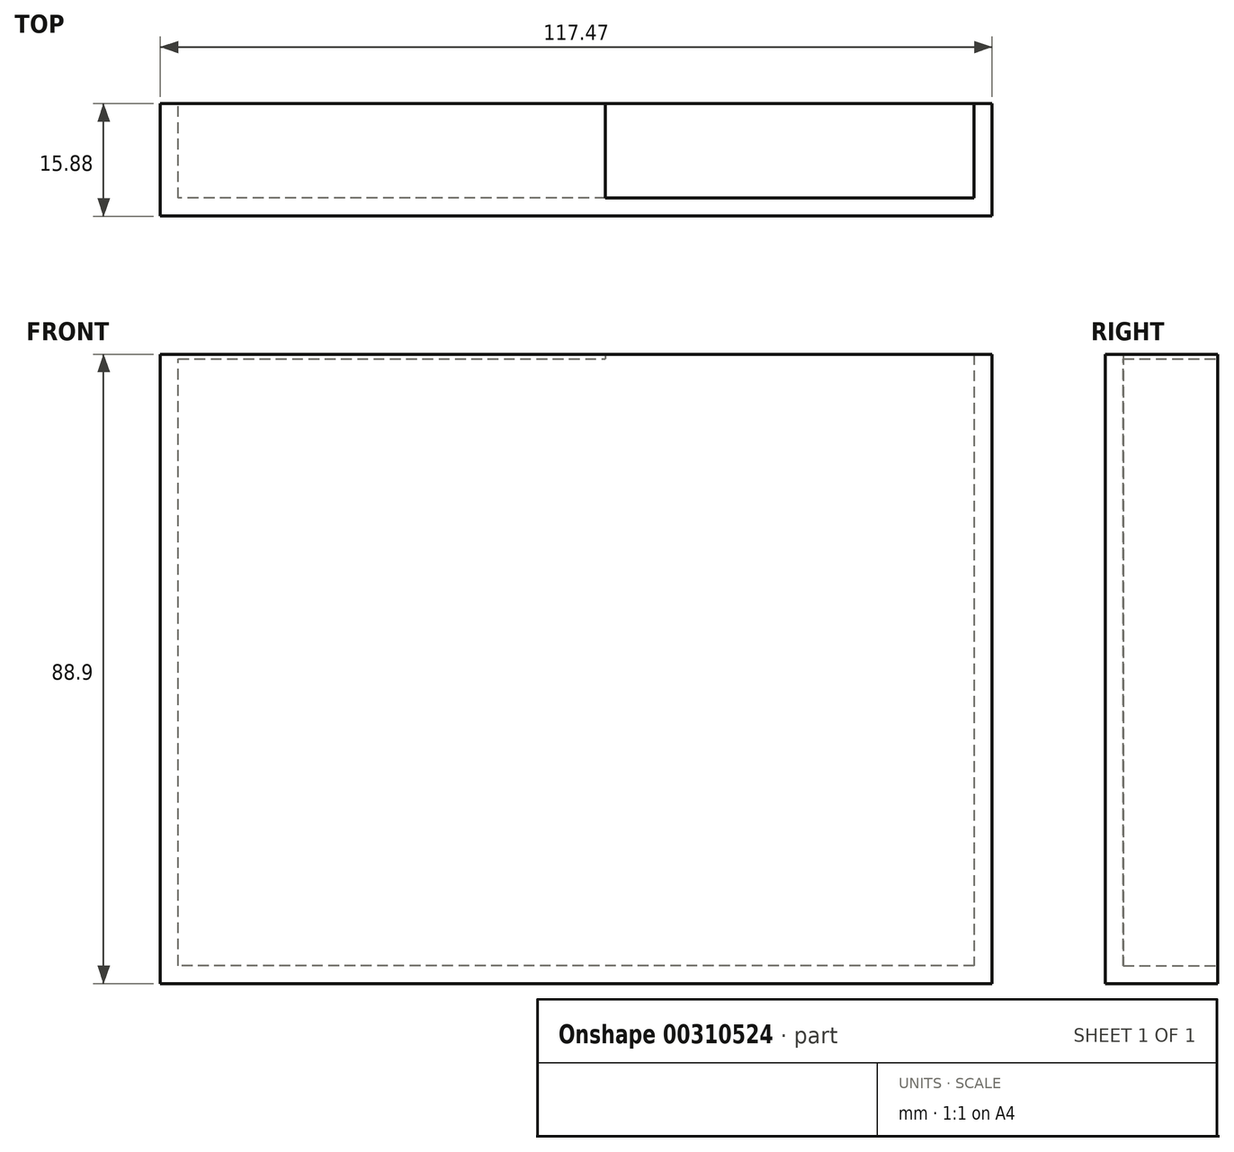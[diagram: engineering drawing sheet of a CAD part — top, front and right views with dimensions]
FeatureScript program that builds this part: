
annotation { "Feature Type Name" : "Feature", "Feature Type Description" : "" }
export const myFeature = defineFeature(function(context is Context, id is Id, definition is map)
    precondition{}
    {
        {
            var Q0;
            Q0=qCreatedBy(makeId("Front.planeOp"),FACE);
            var sketch = newSketch(context, id + "F0", { "sketchPlane" : qUnion([Q0])});
            skLineSegment(sketch, "E0", {"start": v(0, 0) * mm, "end": v(-117.47, 0) * mm});
            skLineSegment(sketch, "E1", {"start": v(0, 0) * mm, "end": v(0, -88.9) * mm});
            skLineSegment(sketch, "E2", {"start": v(0, -88.9) * mm, "end": v(-117.47, -88.9) * mm});
            skLineSegment(sketch, "E3", {"start": v(-117.47, -88.9) * mm, "end": v(-117.47, 0) * mm});
            skSolve(sketch);
        }
        {
            var Q0;
            Q0=makeQuery(id+"F0.imprint","IMPRINT",FACE,{"disambiguationData":[TD([[makeQuery(id+"F0.imprint","IMPRINT",EDGE,{"derivedFrom":sQuery(id+"F0.wireOp",EDGE,"E0")}),1.0]])]});
            extrude(context, id + "F1", {"entities" : qUnion([Q0]), "depth" : 15.88 * mm});
        }
        {
            var Q0;
            Q0=makeQuery(id+"F1.opExtrude","CAP_FACE",FACE,{"disambiguationData":[OSD([sQuery(id+"F0.wireOp",EDGE,"E0"),sQuery(id+"F0.wireOp",EDGE,"E1"),sQuery(id+"F0.wireOp",EDGE,"E2"),sQuery(id+"F0.wireOp",EDGE,"E3")])],"isStart":true});
            var Q1;
            Q1=makeQuery(id+"F1.opExtrude","SWEPT_FACE",FACE,{"disambiguationData":[OSD([sQuery(id+"F0.wireOp",EDGE,"E0")])]});
            shell(context, id + "F2", {"entities" : qUnion([Q0, Q1]), "thickness" : 2.54 * mm});
        }
        {
            var Q0;
            Q0=qCreatedBy(makeId("Front.planeOp"),FACE);
            var sketch = newSketch(context, id + "F3", { "sketchPlane" : qUnion([Q0])});
            skPoint(sketch, "E4.0", {"position": v(-117.47, 0) * mm});
            skPoint(sketch, "E5.0", {"position": v(-114.94, 0) * mm});
            skLineSegment(sketch, "E6.bottom", {"start": v(-114.94, 0) * mm, "end": v(-54.6, 0) * mm});
            skLineSegment(sketch, "E6.top", {"start": v(-114.94, -0.64) * mm, "end": v(-54.6, -0.64) * mm});
            skLineSegment(sketch, "E6.left", {"start": v(-114.94, 0) * mm, "end": v(-114.94, -0.64) * mm});
            skLineSegment(sketch, "E6.right", {"start": v(-54.6, 0) * mm, "end": v(-54.6, -0.64) * mm});
            skSolve(sketch);
        }
        {
            var Q0;
            Q0=makeQuery(id+"F3.imprint","IMPRINT",FACE,{"disambiguationData":[TD([[makeQuery(id+"F3.imprint","IMPRINT",EDGE,{"derivedFrom":sQuery(id+"F3.wireOp",EDGE,"E6.bottom")}),-1.0]])]});
            extrude(context, id + "F4", {"entities" : qUnion([Q0]), "operationType" : NewBodyOperationType.ADD, "endBound" : BoundingType.UP_TO_NEXT, "depth" : 25.4 * mm});
        }
    });
